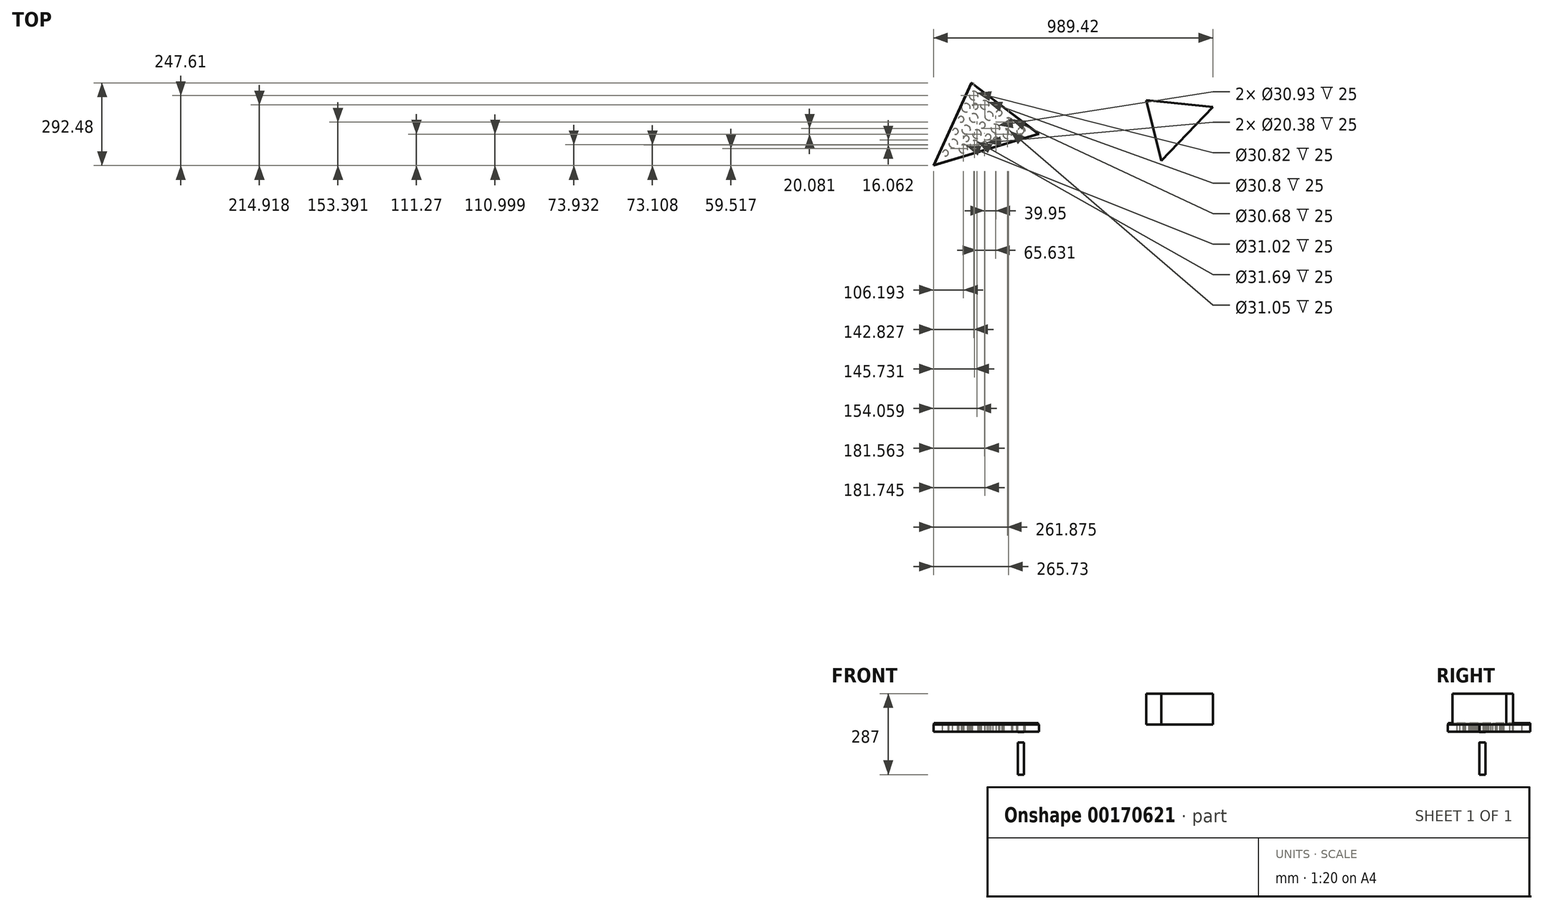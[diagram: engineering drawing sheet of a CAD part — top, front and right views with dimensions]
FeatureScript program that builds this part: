
annotation { "Feature Type Name" : "Feature", "Feature Type Description" : "" }
export const myFeature = defineFeature(function(context is Context, id is Id, definition is map)
    precondition{}
    {
        {
            var Q0;
            Q0=qCreatedBy(makeId("Top.planeOp"),FACE);
            var sketch = newSketch(context, id + "F0", { "sketchPlane" : qUnion([Q0])});
            skLineSegment(sketch, "E0", {"start": v(263.58, -89.58) * mm, "end": v(316.84, -303.75) * mm});
            skLineSegment(sketch, "E1", {"start": v(316.84, -303.75) * mm, "end": v(498.83, -112.88) * mm});
            skLineSegment(sketch, "E2", {"start": v(498.83, -112.88) * mm, "end": v(263.58, -89.58) * mm});
            skSolve(sketch);
        }
        {
            var Q0;
            Q0=makeQuery(id+"F0.imprint","IMPRINT",FACE,{"disambiguationData":[TD([[makeQuery(id+"F0.imprint","IMPRINT",EDGE,{"derivedFrom":sQuery(id+"F0.wireOp",EDGE,"E0")}),1.0]])]});
            extrude(context, id + "F1", {"entities" : qUnion([Q0]), "depth" : 110 * mm});
        }
        {
            var Q0;
            Q0=qCreatedBy(makeId("Top.planeOp"),FACE);
            var sketch = newSketch(context, id + "F2", { "sketchPlane" : qUnion([Q0])});
            skLineSegment(sketch, "E3", {"start": v(-356.45, -28.24) * mm, "end": v(-490.6, -320.72) * mm});
            skLineSegment(sketch, "E4", {"start": v(-490.6, -320.72) * mm, "end": v(-116.75, -208.57) * mm});
            skLineSegment(sketch, "E5", {"start": v(-116.75, -208.57) * mm, "end": v(-356.45, -28.24) * mm});
            skCircle(sketch, "E6", {"center": v(-347.76, -73.11) * mm, "radius": 15.41 * mm});
            skCircle(sketch, "E7", {"center": v(-375.27, -116.18) * mm, "radius": 15.13 * mm});
            skCircle(sketch, "E8", {"center": v(-308.84, -105.8) * mm, "radius": 15.4 * mm});
            skCircle(sketch, "E9", {"center": v(-347.76, -151.88) * mm, "radius": 15.1 * mm});
            skCircle(sketch, "E10", {"center": v(-293.77, -145.35) * mm, "radius": 15.04 * mm});
            skCircle(sketch, "E11", {"center": v(-392.82, -157.11) * mm, "radius": 10.32 * mm});
            skCircle(sketch, "E12", {"center": v(-257.81, -134.56) * mm, "radius": 10.13 * mm});
            skCircle(sketch, "E13", {"center": v(-317.48, -177.8) * mm, "radius": 10.4 * mm});
            skCircle(sketch, "E14", {"center": v(-342.3, -111.33) * mm, "radius": 10.07 * mm});
            skCircle(sketch, "E15", {"center": v(-374.93, -193.6) * mm, "radius": 15.28 * mm});
            skCircle(sketch, "E16", {"center": v(-412.84, -200.07) * mm, "radius": 10.24 * mm});
            skCircle(sketch, "E17", {"center": v(-336.53, -209.45) * mm, "radius": 15.47 * mm});
            skCircle(sketch, "E18", {"center": v(-270.9, -189.37) * mm, "radius": 15.47 * mm});
            skCircle(sketch, "E19", {"center": v(-224.86, -167.33) * mm, "radius": 15.34 * mm});
            skCircle(sketch, "E20", {"center": v(-419.8, -243.25) * mm, "radius": 15.25 * mm});
            skCircle(sketch, "E21", {"center": v(-374.24, -225.61) * mm, "radius": 10.1 * mm});
            skCircle(sketch, "E22", {"center": v(-447.76, -276.6) * mm, "radius": 10.3 * mm});
            skCircle(sketch, "E23", {"center": v(-296.67, -219.6) * mm, "radius": 10.03 * mm});
            skCircle(sketch, "E24", {"center": v(-384.4, -261.2) * mm, "radius": 15.5 * mm});
            skCircle(sketch, "E25", {"center": v(-344.86, -247.61) * mm, "radius": 15.84 * mm});
            skCircle(sketch, "E26", {"center": v(-228.71, -209.72) * mm, "radius": 15.53 * mm});
            skCircle(sketch, "E27", {"center": v(-269.08, -230.73) * mm, "radius": 10.19 * mm});
            skCircle(sketch, "E28", {"center": v(-309.03, -246.79) * mm, "radius": 10.19 * mm});
            skCircle(sketch, "E29", {"center": v(-180.6, -197.59) * mm, "radius": 15.1 * mm});
            skSolve(sketch);
        }
        {
            var Q0;
            Q0 = qSketchRegion(id + "F2", true);
            extrude(context, id + "F3", {"entities" : qUnion([Q0]), "oppositeDirection" : true, "depth" : 25 * mm});
        }
        {
            var Q0;
            Q0=qCreatedBy(makeId("Top.planeOp"),FACE);
            var sketch = newSketch(context, id + "F4", { "sketchPlane" : qUnion([Q0])});
            skLineSegment(sketch, "E30", {"start": v(-118.53, -208.45) * mm, "end": v(-355.88, -28.56) * mm});
            skLineSegment(sketch, "E31", {"start": v(-355.88, -28.56) * mm, "end": v(-488.09, -318.73) * mm});
            skLineSegment(sketch, "E32", {"start": v(-488.09, -318.73) * mm, "end": v(-118.53, -208.45) * mm});
            skSolve(sketch);
        }
        {
            var Q0;
            Q0 = qSketchRegion(id + "F4", true);
            extrude(context, id + "F5", {"entities" : qUnion([Q0]), "operationType" : NewBodyOperationType.ADD, "depth" : 5 * mm});
        }
        {
            var Q0;
            Q0=qCreatedBy(makeId("Top.planeOp"),FACE);
            var sketch = newSketch(context, id + "F6", { "sketchPlane" : qUnion([Q0])});
            skCircle(sketch, "E33", {"center": v(-180.82, -197.68) * mm, "radius": 10.84 * mm});
            skSolve(sketch);
        }
        {
            var Q0;
            Q0 = qSketchRegion(id + "F6", true);
            extrude(context, id + "F7", {"entities" : qUnion([Q0]), "operationType" : NewBodyOperationType.ADD, "oppositeDirection" : true, "depth" : 177 * mm});
        }
        {
            var Q0;
            Q0=qCreatedBy(makeId("Front.planeOp"),FACE);
            var sketch = newSketch(context, id + "F8", { "sketchPlane" : qUnion([Q0])});
            skLineSegment(sketch, "E34.bottom", {"start": v(-231.1, -62.59) * mm, "end": v(-131.8, -62.59) * mm});
            skLineSegment(sketch, "E34.top", {"start": v(-231.1, -26.3) * mm, "end": v(-131.8, -26.3) * mm});
            skLineSegment(sketch, "E34.left", {"start": v(-231.1, -62.59) * mm, "end": v(-231.1, -26.3) * mm});
            skLineSegment(sketch, "E34.right", {"start": v(-131.8, -62.59) * mm, "end": v(-131.8, -26.3) * mm});
            skSolve(sketch);
        }
        {
            var Q0;
            Q0 = qSketchRegion(id + "F8", true);
            extrude(context, id + "F9", {"entities" : qUnion([Q0]), "operationType" : NewBodyOperationType.REMOVE, "depth" : 407 * mm});
        }
    });
